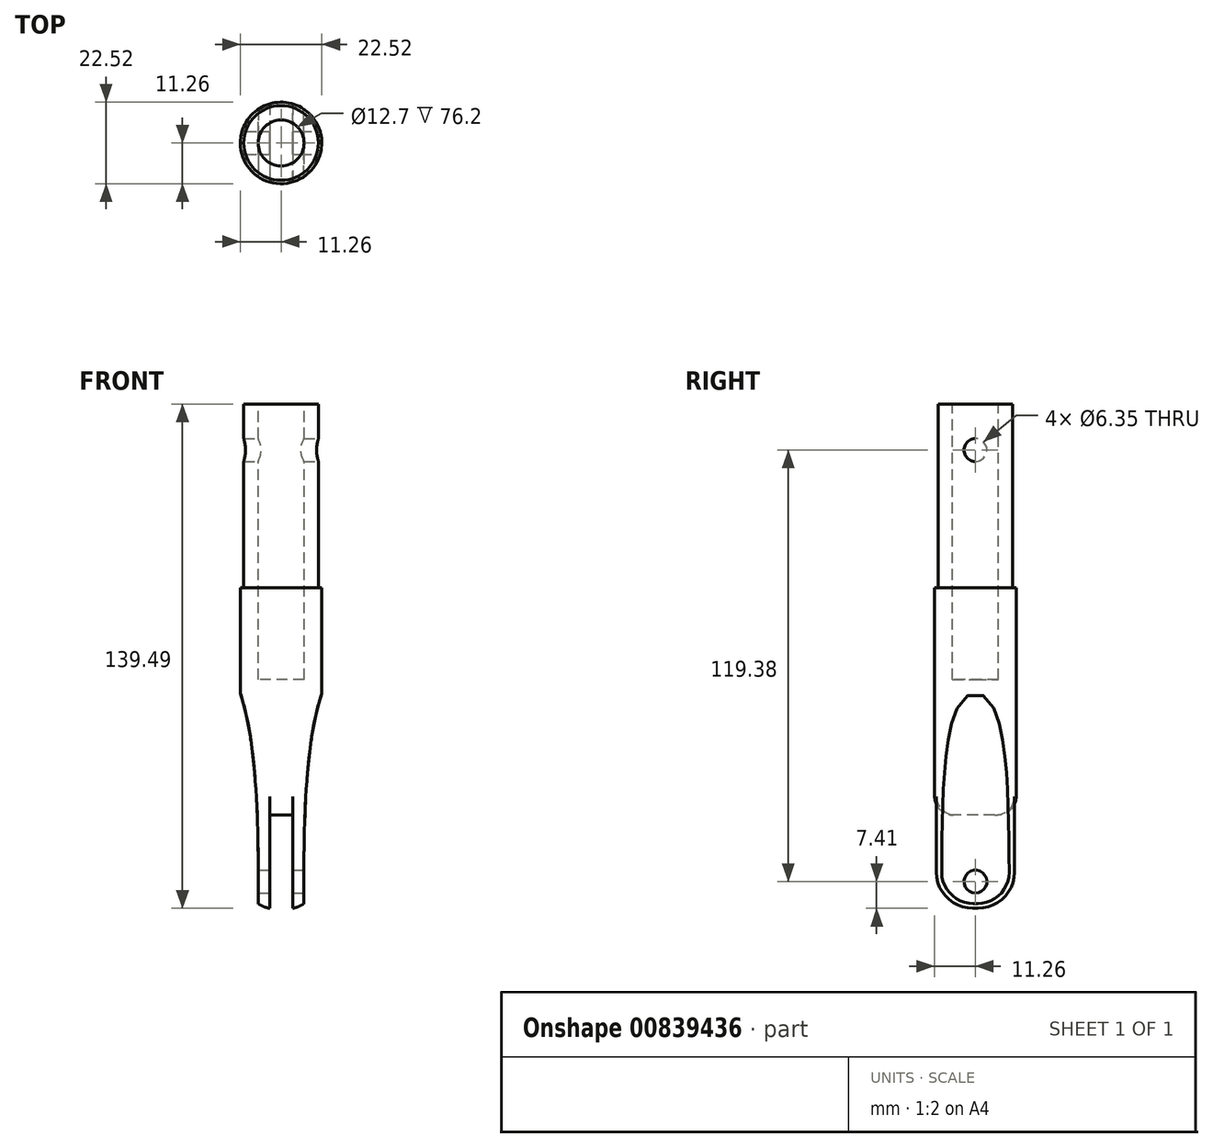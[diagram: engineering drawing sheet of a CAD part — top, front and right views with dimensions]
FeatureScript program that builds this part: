
annotation { "Feature Type Name" : "Feature", "Feature Type Description" : "" }
export const myFeature = defineFeature(function(context is Context, id is Id, definition is map)
    precondition{}
    {
        {
            var Q0;
            Q0=qCreatedBy(makeId("Top.planeOp"),FACE);
            var sketch = newSketch(context, id + "F0", { "sketchPlane" : qUnion([Q0])});
            skCircle(sketch, "E0", {"center": v(0, 0) * mm, "radius": 10.33 * mm});
            skSolve(sketch);
        }
        {
            var Q0;
            Q0 = qSketchRegion(id + "F0", true);
            extrude(context, id + "F1", {"entities" : qUnion([Q0]), "depth" : 50.8 * mm, "offsetDistance" : 25.4 * mm});
        }
        {
            var Q0;
            Q0=makeQuery(id+"F1.opExtrude","CAP_FACE",FACE,{"disambiguationData":[OSD([sQuery(id+"F0.wireOp",EDGE,"E0")])],"isStart":true});
            var sketch = newSketch(context, id + "F2", { "sketchPlane" : qUnion([Q0])});
            skCircle(sketch, "E1", {"center": v(0, 0) * mm, "radius": 11.26 * mm});
            skSolve(sketch);
        }
        {
            var Q0;
            Q0 = qSketchRegion(id + "F2", true);
            extrude(context, id + "F3", {"entities" : qUnion([Q0]), "operationType" : NewBodyOperationType.ADD, "depth" : 88.9 * mm, "offsetDistance" : 25.4 * mm});
        }
        {
            var Q0;
            Q0=qCreatedBy(makeId("Right.planeOp"),FACE);
            var sketch = newSketch(context, id + "F4", { "sketchPlane" : qUnion([Q0])});
            skCircle(sketch, "E2", {"center": v(0, 38.1) * mm, "radius": 3.18 * mm});
            skSolve(sketch);
        }
        {
            var Q0;
            Q0 = qSketchRegion(id + "F4", true);
            extrude(context, id + "F5", {"entities" : qUnion([Q0]), "operationType" : NewBodyOperationType.REMOVE, "endBound" : BoundingType.THROUGH_ALL, "oppositeDirection" : true, "depth" : 25.4 * mm, "offsetDistance" : 25.4 * mm, "hasSecondDirection" : true, "secondDirectionBound" : BoundingType.THROUGH_ALL, "secondDirectionOppositeDirection" : false, "secondDirectionDepth" : 25.4 * mm});
        }
        {
            var Q0;
            Q0=qCreatedBy(makeId("Front.planeOp"),FACE);
            var sketch = newSketch(context, id + "F6", { "sketchPlane" : qUnion([Q0])});
            skLineSegment(sketch, "E3", {"start": v(0, -101.6) * mm, "end": v(3.18, -101.6) * mm, "construction": true});
            skLineSegment(sketch, "E4", {"start": v(0, -101.6) * mm, "end": v(-6.35, -101.6) * mm, "construction": true});
            skLineSegment(sketch, "E5.bottom", {"start": v(-6.35, -101.6) * mm, "end": v(-19.05, -101.6) * mm});
            skLineSegment(sketch, "E5.top", {"start": v(-6.35, -88.9) * mm, "end": v(-19.05, -88.9) * mm});
            skLineSegment(sketch, "E5.left", {"start": v(-6.35, -101.6) * mm, "end": v(-6.35, -88.9) * mm});
            skLineSegment(sketch, "E5.right", {"start": v(-19.05, -101.6) * mm, "end": v(-19.05, -88.9) * mm});
            skLineSegment(sketch, "E6.MirrorCS", {"start": v(6.35, -88.9) * mm, "end": v(19.05, -88.9) * mm});
            skLineSegment(sketch, "E7.MirrorCS", {"start": v(6.35, -101.6) * mm, "end": v(6.35, -88.9) * mm});
            skLineSegment(sketch, "E8.MirrorCS", {"start": v(6.35, -101.6) * mm, "end": v(19.05, -101.6) * mm});
            skLineSegment(sketch, "E9.MirrorCS", {"start": v(19.05, -101.6) * mm, "end": v(19.05, -88.9) * mm});
            skLineSegment(sketch, "E10", {"start": v(0, 0) * mm, "end": v(0, -25.4) * mm, "construction": true});
            skLineSegment(sketch, "E11", {"start": v(0, -25.4) * mm, "end": v(-12.7, -25.4) * mm, "construction": true});
            skLineSegment(sketch, "E12.MirrorCS", {"start": v(0, -25.4) * mm, "end": v(12.7, -25.4) * mm, "construction": true});
            skFitSpline(sketch, "E13", {"points": [v(-12.7, -25.4) * mm, v(-6.35, -88.9) * mm], "startDerivative": vector(18.42, -41.8) * mm, "endDerivative": vector(-0.74, -72.86) * mm});
            skFitSpline(sketch, "E14.MirrorCS", {"points": [v(12.7, -25.4) * mm, v(6.35, -88.9) * mm], "startDerivative": vector(-18.42, -41.8) * mm, "endDerivative": vector(0.74, -72.86) * mm});
            skLineSegment(sketch, "E15", {"start": v(-12.7, -25.4) * mm, "end": v(-19.05, -88.9) * mm});
            skLineSegment(sketch, "E16", {"start": v(12.7, -25.4) * mm, "end": v(19.05, -88.9) * mm});
            skSolve(sketch);
        }
        {
            var Q0;
            Q0 = qSketchRegion(id + "F6", true);
            extrude(context, id + "F7", {"entities" : qUnion([Q0]), "operationType" : NewBodyOperationType.REMOVE, "endBound" : BoundingType.THROUGH_ALL, "oppositeDirection" : true, "depth" : 25.4 * mm, "offsetDistance" : 25.4 * mm, "hasSecondDirection" : true, "secondDirectionBound" : BoundingType.THROUGH_ALL, "secondDirectionOppositeDirection" : false, "secondDirectionDepth" : 25.4 * mm});
        }
        {
            var Q0;
            Q0=qCreatedBy(makeId("Right.planeOp"),FACE);
            var sketch = newSketch(context, id + "F8", { "sketchPlane" : qUnion([Q0])});
            skCircle(sketch, "E17", {"center": v(0, -81.28) * mm, "radius": 3.18 * mm});
            skSolve(sketch);
        }
        {
            var Q0;
            Q0 = qSketchRegion(id + "F8", true);
            extrude(context, id + "F9", {"entities" : qUnion([Q0]), "operationType" : NewBodyOperationType.REMOVE, "endBound" : BoundingType.THROUGH_ALL, "oppositeDirection" : true, "depth" : 25.4 * mm, "offsetDistance" : 25.4 * mm, "hasSecondDirection" : true, "secondDirectionBound" : BoundingType.THROUGH_ALL, "secondDirectionOppositeDirection" : false, "secondDirectionDepth" : 25.4 * mm});
        }
        {
            var Q0;
            Q0=makeQuery(id+"F7.boolean.opBoolean","SPLIT",EDGE,{"disambiguationData":[OD(1.0)],"derivedFrom":makeQuery(id+"F3.opExtrude","CAP_EDGE",EDGE,{"disambiguationData":[OSD([sQuery(id+"F2.wireOp",EDGE,"E1")])],"isStart":false})});
            var Q1;
            Q1=makeQuery(id+"F7.boolean.opBoolean","SPLIT",EDGE,{"disambiguationData":[OD(0.0)],"derivedFrom":makeQuery(id+"F3.opExtrude","CAP_EDGE",EDGE,{"disambiguationData":[OSD([sQuery(id+"F2.wireOp",EDGE,"E1")])],"isStart":false})});
            fillet(context, id + "F10", {"entities" : qUnion([Q0, Q1]), "tangentPropagation" : true, "radius" : 10.16 * mm, "defaultsChanged" : true, "vertexSettings" : [], "allowEdgeOverflow" : false});
        }
        {
            var Q0;
            Q0=makeQuery(id+"F1.opExtrude","CAP_FACE",FACE,{"disambiguationData":[OSD([sQuery(id+"F0.wireOp",EDGE,"E0")])],"isStart":false});
            var sketch = newSketch(context, id + "F11", { "sketchPlane" : qUnion([Q0])});
            skCircle(sketch, "E18", {"center": v(0, 0) * mm, "radius": 6.35 * mm});
            skSolve(sketch);
        }
        {
            var Q0;
            Q0 = qSketchRegion(id + "F11", true);
            extrude(context, id + "F12", {"entities" : qUnion([Q0]), "operationType" : NewBodyOperationType.REMOVE, "oppositeDirection" : true, "depth" : 76.2 * mm, "offsetDistance" : 25.4 * mm});
        }
        {
            var Q0;
            Q0=qCreatedBy(makeId("Front.planeOp"),FACE);
            var sketch = newSketch(context, id + "F13", { "sketchPlane" : qUnion([Q0])});
            skLineSegment(sketch, "E19.bottom", {"start": v(3.18, -94.62) * mm, "end": v(-3.17, -94.62) * mm});
            skLineSegment(sketch, "E19.top", {"start": v(3.18, -62.87) * mm, "end": v(-3.17, -62.87) * mm});
            skLineSegment(sketch, "E19.left", {"start": v(3.18, -94.62) * mm, "end": v(3.18, -62.87) * mm});
            skLineSegment(sketch, "E19.right", {"start": v(-3.17, -94.62) * mm, "end": v(-3.17, -62.87) * mm});
            skPoint(sketch, "E19.middle", {"position": v(0, -78.74) * mm});
            skSolve(sketch);
        }
        {
            var Q0;
            Q0 = qSketchRegion(id + "F13", true);
            extrude(context, id + "F14", {"entities" : qUnion([Q0]), "operationType" : NewBodyOperationType.REMOVE, "endBound" : BoundingType.THROUGH_ALL, "oppositeDirection" : true, "depth" : 25.4 * mm, "offsetDistance" : 25.4 * mm, "hasSecondDirection" : true, "secondDirectionBound" : BoundingType.THROUGH_ALL, "secondDirectionOppositeDirection" : false, "secondDirectionDepth" : 25.4 * mm});
        }
        {
            var Q0;
            Q0=makeQuery(id+"F14.boolean.opBoolean","INTERSECT",EDGE,{"disambiguationData":[OD(0.0)],"derivedFrom":[makeQuery(id+"F3.opExtrude","SWEPT_FACE",FACE,{"disambiguationData":[OSD([sQuery(id+"F2.wireOp",EDGE,"E1")])]}),makeQuery(id+"F14.opExtrude","SWEPT_FACE",FACE,{"disambiguationData":[OSD([sQuery(id+"F13.wireOp",EDGE,"E19.top")])]})]});
            var Q1;
            Q1=makeQuery(id+"F14.boolean.opBoolean","INTERSECT",EDGE,{"disambiguationData":[OD(1.0)],"derivedFrom":[makeQuery(id+"F3.opExtrude","SWEPT_FACE",FACE,{"disambiguationData":[OSD([sQuery(id+"F2.wireOp",EDGE,"E1")])]}),makeQuery(id+"F14.opExtrude","SWEPT_FACE",FACE,{"disambiguationData":[OSD([sQuery(id+"F13.wireOp",EDGE,"E19.top")])]})]});
            fillet(context, id + "F15", {"entities" : qUnion([Q0, Q1]), "tangentPropagation" : true, "radius" : 5.08 * mm, "defaultsChanged" : false, "vertexSettings" : [], "allowEdgeOverflow" : false});
        }
    });
